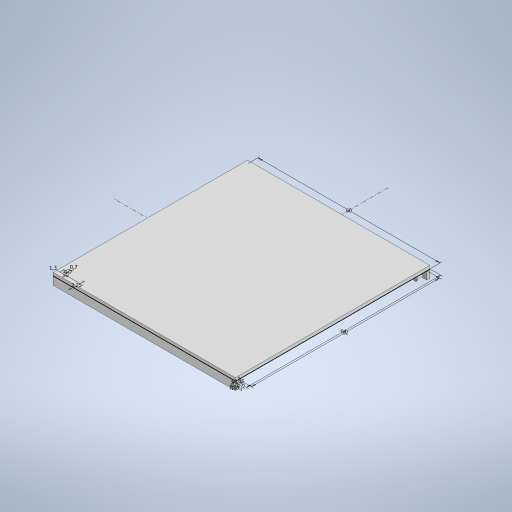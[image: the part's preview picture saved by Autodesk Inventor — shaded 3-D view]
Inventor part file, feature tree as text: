
AUTODESK INVENTOR PART (.ipt)
format: ipt  version: 2023 (Build 270158000, 158)  size: 276,480 bytes
history: native  units: mm
features: extrude x6, sketch x3
ambient origin geometry x8: Origin, YZ Plane, XZ Plane, XY Plane, X Axis, Y Axis, Z Axis, Center Point
bodies: Solido1 (feature_tree)
feature tree (9):
  sketch  "Schizzo1"
  extrude  "Estrusione1"  Depth=60.0mm
  extrude  "Estrusione2"  Depth=64.0mm
  sketch  "Schizzo2"
  extrude  "Estrusione3"  Depth=2.25mm
  extrude  "Estrusione4"  Depth=1.2mm
  sketch  "Schizzo3"
  extrude  "Estrusione5"  Depth=0.7mm
  extrude  "Estrusione6"  Depth=0.7mm
